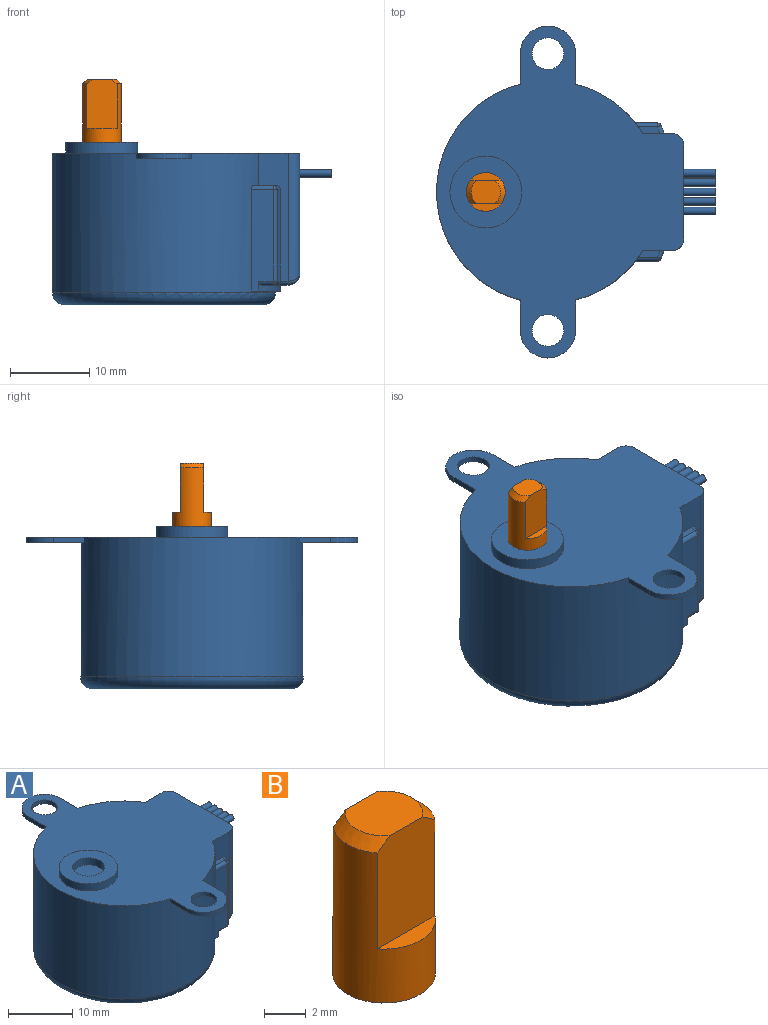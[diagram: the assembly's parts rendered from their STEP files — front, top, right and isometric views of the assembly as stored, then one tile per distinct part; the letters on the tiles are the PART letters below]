
ASSEMBLY  parts=2 mates=1
PART A: 70 faces, bbox 36.5x42x20.6 mm
  f0: plane 15.2x11.8mm, normal (1,0,0), area 169.8mm2, adj f14,f29,f30,f31,f51,f52,f53,f54
  f1: cylinder r=14.1mm len=28.2mm, axis (0,0,1), area 1244mm2, adj f2,f3,f4,f5,f6,f7,f8,f13
  f2: plane 16.5x3.36mm, normal (0,0,-1), area 25.3mm2, adj f1,f23,f24,f26,f27,f30,f37,f39
  f3: plane 16.2x3.7mm, normal (0,1,0), area 27.3mm2, adj f1,f14,f17,f18,f29,f33,f40
  f4: plane 3.84x0.75mm, normal (-1,0,0), area 2.9mm2, adj f1,f10,f13,f14
  f5: plane 3.84x0.75mm, normal (-1,0,0), area 2.9mm2, adj f1,f8,f9,f14
  f6: plane 3.84x0.75mm, normal (1,0,0), area 2.9mm2, adj f1,f10,f13,f14
  f7: plane 3.84x0.75mm, normal (1,0,0), area 2.9mm2, adj f1,f8,f9,f14
  f8: plane 7.34x7mm, normal (0,0,-1), area 31.5mm2, adj f1,f5,f7,f9,f12
  f9: cylinder r=3.5mm len=7mm, axis (0,0,1), area 8.2mm2, adj f5,f7,f8,f14
  f10: cylinder r=3.5mm len=7mm, axis (0,0,1), area 8.2mm2, adj f4,f6,f13,f14
  f11: cylinder r=2mm len=4mm, axis (0,0,1), area 9.4mm2, adj f13,f14
  f12: cylinder r=2mm len=4mm, axis (0,0,1), area 9.4mm2, adj f8,f14
  f13: plane 7.34x7mm, normal (0,0,-1), area 31.5mm2, adj f1,f4,f6,f10,f11
  f14: plane 42x31.3mm, normal (0,0,1), area 677.5mm2, adj f0,f1,f3,f4,f5,f6,f7,f9
  f15: plane 25.2x25.2mm, normal (0,0,-1), area 498.8mm2, adj f32
  f16: plane 16.2x3.7mm, normal (0,-1,0), area 27.3mm2, adj f1,f14,f20,f21,f31,f43,f49
  f17: plane 2.73x0.85mm, normal (0,0,1), area 1.9mm2, adj f1,f3,f33,f34
  f18: plane 11.6x1.02mm, normal (0.94,0.35,0), area 12.7mm2, adj f3,f33,f36,f39
  f19: plane 12.85x2.8mm, normal (0,1,0), area 33.6mm2, adj f1,f24,f25,f34,f36,f37
  f20: plane 2.73x0.85mm, normal (0,0,1), area 1.9mm2, adj f1,f16,f42,f43
  f21: plane 11.6x1.02mm, normal (0.94,-0.35,0), area 12.7mm2, adj f16,f43,f46,f48
  f22: plane 12.85x2.8mm, normal (0,-1,0), area 33.6mm2, adj f1,f26,f28,f42,f45,f46
  f23: plane 0.75x0.75mm, normal (0,-1,0), area 0.6mm2, adj f1,f2,f24,f25
  f24: cylinder r=14.85mm len=7.25mm, axis (0,0,1), area 6mm2, adj f2,f19,f23,f25,f37
  f25: plane 7.25x3.71mm, normal (0,0,-1), area 5.9mm2, adj f1,f19,f23,f24
  f26: cylinder r=14.85mm len=7.25mm, axis (0,0,1), area 6mm2, adj f2,f22,f27,f28,f45
  f27: plane 0.75x0.75mm, normal (0,1,0), area 0.6mm2, adj f1,f2,f26,f28
  f28: plane 7.25x3.71mm, normal (0,0,-1), area 5.9mm2, adj f1,f22,f26,f27
  f29: cylinder r=1.5mm len=16.2mm, axis (0,0,-1), area 37.3mm2, adj f0,f3,f14,f41
  f30: cylinder r=1.5mm len=13.8mm, axis (0,-1,0), area 30.8mm2, adj f0,f2,f41,f50
  f31: cylinder r=1.5mm len=16.2mm, axis (0,0,1), area 37.3mm2, adj f0,f14,f16,f50
  f32: torus R=12.6mm, axis (0,0,-1), area 200.7mm2, adj f1,f15
  f33: cylinder r=0.5mm len=1.2mm, axis (-0.35,0.94,0), area 0.8mm2, adj f3,f17,f18,f35
  f34: cylinder r=0.5mm len=2.8mm, axis (-1,0,0), area 2.1mm2, adj f1,f17,f19,f35
  f35: sphere r=0.5mm, area 0.3mm2, adj f33,f34,f36
  f36: cylinder r=0.5mm len=11.6mm, axis (0,0,-1), area 7.1mm2, adj f18,f19,f35,f38
  f37: cylinder r=0.5mm len=1.86mm, axis (-1,0,0), area 1.4mm2, adj f2,f19,f24,f38
  f38: sphere r=0.5mm, area 0.3mm2, adj f36,f37,f39
  f39: cylinder r=0.5mm len=1.52mm, axis (-0.35,0.94,0), area 1mm2, adj f2,f18,f38,f40
  f40: cylinder r=0.5mm len=1.35mm, axis (1,0,0), area 0.9mm2, adj f2,f3,f39,f41
  f41: bspline ~1.76x1.5mm, area 1.3mm2, adj f29,f30,f40
  f42: cylinder r=0.5mm len=2.8mm, axis (1,0,0), area 2.1mm2, adj f1,f20,f22,f44
  f43: cylinder r=0.5mm len=1.2mm, axis (0.35,0.94,0), area 0.8mm2, adj f16,f20,f21,f44
  f44: sphere r=0.5mm, area 0.3mm2, adj f42,f43,f46
  f45: cylinder r=0.5mm len=1.86mm, axis (1,0,0), area 1.4mm2, adj f2,f22,f26,f47
  f46: cylinder r=0.5mm len=11.6mm, axis (0,0,-1), area 7.1mm2, adj f21,f22,f44,f47
  f47: sphere r=0.5mm, area 0.3mm2, adj f45,f46,f48
  f48: cylinder r=0.5mm len=1.52mm, axis (0.35,0.94,0), area 1mm2, adj f2,f21,f47,f49
  f49: cylinder r=0.5mm len=1.35mm, axis (-1,0,0), area 0.9mm2, adj f2,f16,f48,f50
  f50: bspline ~1.76x1.5mm, area 1.3mm2, adj f30,f31,f49
  f51: plane 6.3x1mm, normal (0,0,1), area 6.3mm2, adj f0,f52,f54,f55
  f52: cylinder r=0.65mm len=1.3mm, axis (1,0,0), area 2mm2, adj f0,f51,f53,f55
  f53: plane 6.3x1mm, normal (0,0,-1), area 6.3mm2, adj f0,f52,f54,f55
  f54: cylinder r=0.65mm len=1.3mm, axis (1,0,0), area 2mm2, adj f0,f51,f53,f55
  f55: plane 7.6x1.3mm, normal (1,0,0), area 5.6mm2, adj f51,f52,f53,f54,f60,f62,f64,f66
  f56: plane 9.1x9.1mm, normal (0,0,1), area 46.2mm2, adj f57,f58
  f57: cylinder r=2.45mm len=4.9mm, axis (0,0,-1), area 20.8mm2, adj f56,f59
  f58: cylinder r=4.55mm len=9.1mm, axis (0,0,-1), area 38.6mm2, adj f14,f56
  f59: plane 4.9x4.9mm, normal (0,0,1), area 18.9mm2, adj f57
  f60: cylinder r=0.5mm len=5mm, axis (-1,0,0), area 15.7mm2, adj f55,f61
  f61: plane 1x1mm, normal (1,0,0), area 0.8mm2, adj f60
  f62: cylinder r=0.5mm len=5mm, axis (-1,0,0), area 15.7mm2, adj f55,f63
  f63: plane 1x1mm, normal (1,0,0), area 0.8mm2, adj f62
  f64: cylinder r=0.5mm len=5mm, axis (-1,0,0), area 15.7mm2, adj f55,f65
  f65: plane 1x1mm, normal (1,0,0), area 0.8mm2, adj f64
  f66: cylinder r=0.5mm len=5mm, axis (-1,0,0), area 15.7mm2, adj f55,f67
  f67: plane 1x1mm, normal (1,0,0), area 0.8mm2, adj f66
  f68: cylinder r=0.5mm len=5mm, axis (-1,0,0), area 15.7mm2, adj f55,f69
  f69: plane 1x1mm, normal (1,0,0), area 0.8mm2, adj f68
PART B: 9 faces, bbox 5x5x9.5 mm
  f0: cylinder r=2.45mm len=8.75mm, axis (0,0,-1), area 84.7mm2, adj f1,f2,f4,f5,f6,f7,f8
  f1: cone r=1.85mm half-angle=45deg, axis (0,0,-1), area 2.9mm2, adj f0,f3,f6,f8
  f2: cone r=1.85mm half-angle=45deg, axis (0,0,-1), area 2.9mm2, adj f0,f3,f6,f8
  f3: plane 3.7x3mm, normal (0,0,1), area 9.7mm2, adj f1,f2,f6,f8
  f4: plane 4.9x4.9mm, normal (0,0,-1), area 18.9mm2, adj f0
  f5: plane 3.87x0.95mm, normal (0,0,1), area 2.6mm2, adj f0,f6
  f6: plane 6.31x3.98mm, normal (0,-1,0), area 23.5mm2, adj f0,f1,f2,f3,f5
  f7: plane 3.87x0.95mm, normal (0,0,1), area 2.6mm2, adj f0,f8
  f8: plane 6.31x3.98mm, normal (0,1,0), area 23.5mm2, adj f0,f1,f2,f3,f7
PLACE A at identity
PLACE B at identity
MATE revolute B.f0 <-> A.f57  axis (0,0,-1) through (0,0,0)mm
